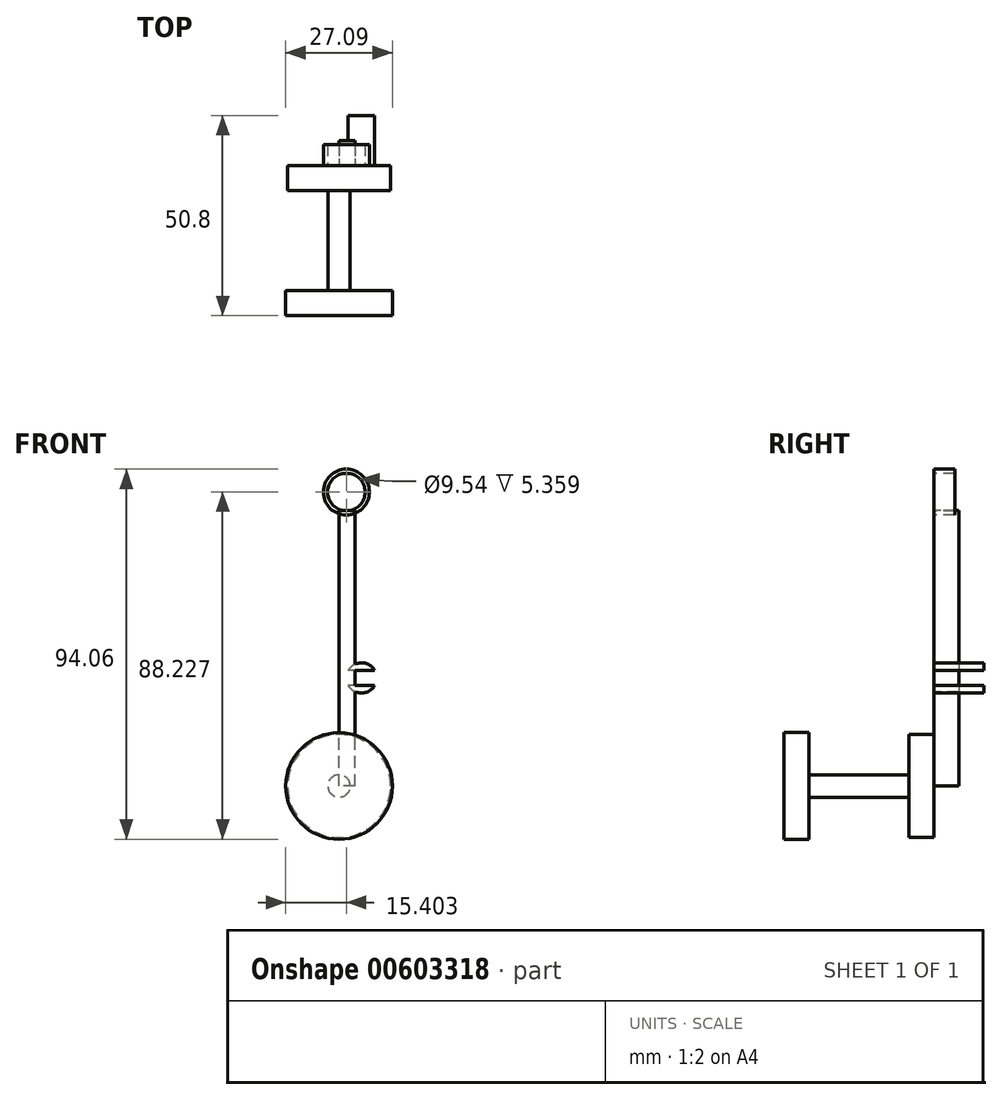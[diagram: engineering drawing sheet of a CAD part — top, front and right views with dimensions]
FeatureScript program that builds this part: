
annotation { "Feature Type Name" : "Feature", "Feature Type Description" : "" }
export const myFeature = defineFeature(function(context is Context, id is Id, definition is map)
    precondition{}
    {
        {
            var Q0;
            Q0=qCreatedBy(makeId("Front.planeOp"),FACE);
            var sketch = newSketch(context, id + "F0", { "sketchPlane" : qUnion([Q0])});
            skLineSegment(sketch, "E0.bottom", {"start": v(-4.93, 2.51) * mm, "end": v(-9.02, 2.51) * mm});
            skLineSegment(sketch, "E0.top", {"start": v(-4.93, 72.47) * mm, "end": v(-9.02, 72.47) * mm});
            skLineSegment(sketch, "E0.left", {"start": v(-4.93, 2.51) * mm, "end": v(-4.93, 72.47) * mm});
            skLineSegment(sketch, "E0.right", {"start": v(-9.02, 2.51) * mm, "end": v(-9.02, 72.47) * mm});
            skCircle(sketch, "E1", {"center": v(-9.02, 2.51) * mm, "radius": 13.09 * mm});
            skArc(sketch, "E2", {"start": v(-14.05, 24.28) * mm, "mid": v(-8.83, 25.1) * mm, "end": v(-13.86, 26.7) * mm});
            skLineSegment(sketch, "E3", {"start": v(-14.05, 24.28) * mm, "end": v(-9.02, 24.28) * mm});
            skLineSegment(sketch, "E4", {"start": v(-13.86, 26.7) * mm, "end": v(-9.21, 26.7) * mm});
            skSolve(sketch);
        }
        {
            var Q0;
            {var subQ0=sQuery(id+"F0.wireOp",EDGE,"E0.bottom");Q0=makeQuery(id+"F0.imprint","IMPRINT",FACE,{"disambiguationData":[TD([[makeQuery(id+"F0.imprint","IMPRINT",EDGE,{"derivedFrom":subQ0}),1.0]])]});}
            var Q1;
            {var subQ0=sQuery(id+"F0.wireOp",EDGE,"E0.bottom");Q1=makeQuery(id+"F0.imprint","IMPRINT",FACE,{"disambiguationData":[TD([[makeQuery(id+"F0.imprint","IMPRINT",EDGE,{"derivedFrom":subQ0}),-1.0]])]});}
            extrude(context, id + "F1", {"entities" : qUnion([Q0, Q1]), "depth" : 6.35 * mm, "offsetDistance" : 25.4 * mm});
        }
        {
            var Q0;
            {var subQ1=sQuery(id+"F0.wireOp",EDGE,"E0.top");Q0=makeQuery(id+"F0.imprint","IMPRINT",FACE,{"disambiguationData":[TD([[makeQuery(id+"F0.imprint","IMPRINT",EDGE,{"derivedFrom":subQ1}),1.0]])]});}
            var Q1;
            {var subQ0=sQuery(id+"F0.wireOp",EDGE,"E0.bottom");Q1=makeQuery(id+"F0.imprint","IMPRINT",FACE,{"disambiguationData":[TD([[makeQuery(id+"F0.imprint","IMPRINT",EDGE,{"derivedFrom":subQ0}),-1.0]])]});}
            var Q2;
            {var subQ0=sQuery(id+"F0.wireOp",EDGE,"E2");var subQ1=sQuery(id+"F0.wireOp",EDGE,"E0.right");var subQ3=makeQuery(id+"F0.imprint","INTERSECT",VERTEX,{"derivedFrom":[subQ1,subQ0]});Q2=makeQuery(id+"F0.imprint","IMPRINT",FACE,{"disambiguationData":[TD([[makeQuery(id+"F0.imprint","IMPRINT",EDGE,{"disambiguationData":[TD([[subQ3,1.0]])],"derivedFrom":subQ1}),-1.0]])]});}
            extrude(context, id + "F2", {"entities" : qUnion([Q0, Q1, Q2]), "oppositeDirection" : true, "depth" : 6.35 * mm, "offsetDistance" : 25.4 * mm});
        }
        {
            var Q0;
            Q0=makeQuery(id+"F1.opExtrude","CAP_FACE",FACE,{"disambiguationData":[OSD([sQuery(id+"F0.wireOp",EDGE,"E1")])],"isStart":false});
            var sketch = newSketch(context, id + "F3", { "sketchPlane" : qUnion([Q0])});
            skCircle(sketch, "E5", {"center": v(-9.02, 2.51) * mm, "radius": 2.84 * mm});
            skSolve(sketch);
        }
        {
            var Q0;
            Q0 = qSketchRegion(id + "F3", true);
            extrude(context, id + "F4", {"entities" : qUnion([Q0]), "operationType" : NewBodyOperationType.ADD, "depth" : 25.4 * mm, "offsetDistance" : 25.4 * mm});
        }
        {
            var Q0;
            Q0=makeQuery(id+"F4.opExtrude","CAP_FACE",FACE,{"disambiguationData":[OSD([sQuery(id+"F3.wireOp",EDGE,"E5")])],"isStart":false});
            var sketch = newSketch(context, id + "F5", { "sketchPlane" : qUnion([Q0])});
            skCircle(sketch, "E6", {"center": v(-9.02, 2.51) * mm, "radius": 13.55 * mm});
            skSolve(sketch);
        }
        {
            var Q0;
            Q0 = qSketchRegion(id + "F5", true);
            extrude(context, id + "F6", {"entities" : qUnion([Q0]), "operationType" : NewBodyOperationType.ADD, "depth" : 6.35 * mm, "offsetDistance" : 25.4 * mm});
        }
        {
            var Q0;
            Q0=qCreatedBy(makeId("Front.planeOp"),FACE);
            var sketch = newSketch(context, id + "F7", { "sketchPlane" : qUnion([Q0])});
            skArc(sketch, "E7", {"start": v(0, 31.86) * mm, "mid": v(-7.19, 29.97) * mm, "end": v(0, 28.07) * mm});
            skLineSegment(sketch, "E8", {"start": v(0, 31.86) * mm, "end": v(-6.69, 31.86) * mm});
            skLineSegment(sketch, "E9", {"start": v(0, 28.07) * mm, "end": v(-6.69, 28.07) * mm});
            skSolve(sketch);
        }
        {
            var Q0;
            Q0=qCreatedBy(makeId("Front.planeOp"),FACE);
            var sketch = newSketch(context, id + "F8", { "sketchPlane" : qUnion([Q0])});
            skCircle(sketch, "E10", {"center": v(-7.17, 77.2) * mm, "radius": 5.84 * mm});
            skCircle(sketch, "E11.0", {"center": v(-7.17, 77.2) * mm, "radius": 4.77 * mm});
            skSolve(sketch);
        }
        {
            var Q0;
            {var subQ0=sQuery(id+"F7.wireOp",EDGE,"E8");Q0=makeQuery(id+"F7.imprint","IMPRINT",FACE,{"disambiguationData":[TD([[makeQuery(id+"F7.imprint","IMPRINT",EDGE,{"derivedFrom":subQ0}),-1.0]])]});}
            var Q1;
            {var subQ0=sQuery(id+"F7.wireOp",EDGE,"E9");Q1=makeQuery(id+"F7.imprint","IMPRINT",FACE,{"disambiguationData":[TD([[makeQuery(id+"F7.imprint","IMPRINT",EDGE,{"derivedFrom":subQ0}),1.0]])]});}
            extrude(context, id + "F9", {"entities" : qUnion([Q0, Q1]), "operationType" : NewBodyOperationType.ADD, "oppositeDirection" : true, "depth" : 12.7 * mm, "offsetDistance" : 25.4 * mm});
        }
        {
            var Q0;
            Q0 = qSketchRegion(id + "F8", true);
            extrude(context, id + "F10", {"entities" : qUnion([Q0]), "oppositeDirection" : true, "depth" : 5.36 * mm, "offsetDistance" : 25.4 * mm});
        }
    });
